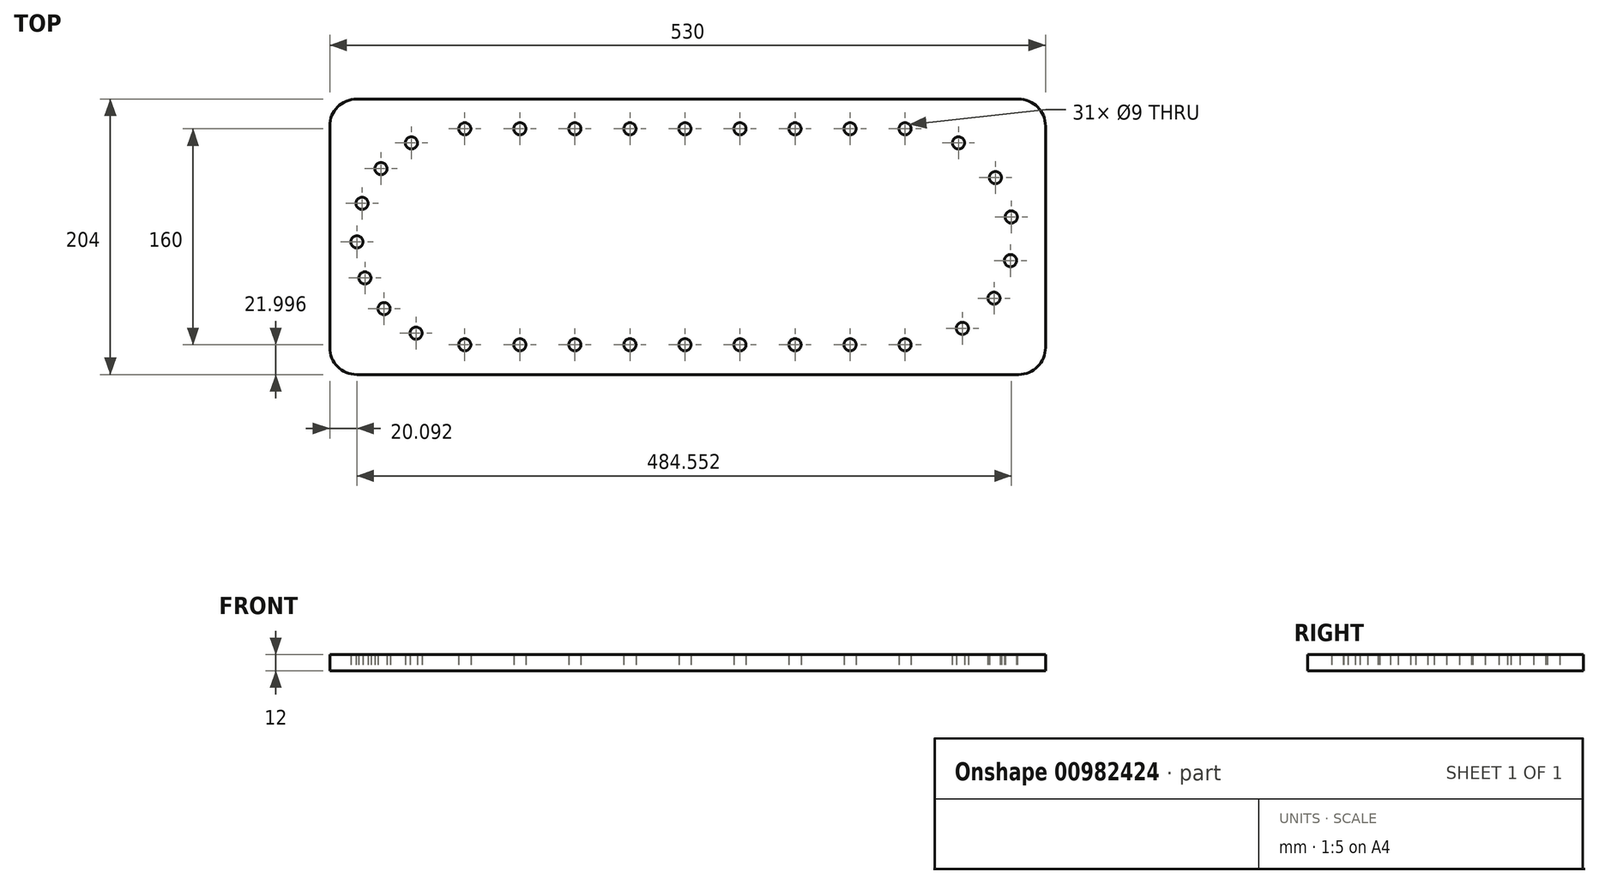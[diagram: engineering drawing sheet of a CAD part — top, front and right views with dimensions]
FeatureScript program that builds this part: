
annotation { "Feature Type Name" : "Feature", "Feature Type Description" : "" }
export const myFeature = defineFeature(function(context is Context, id is Id, definition is map)
    precondition{}
    {
        {
            var Q0;
            Q0=qCreatedBy(makeId("Top.planeOp"),FACE);
            var sketch = newSketch(context, id + "F0", { "sketchPlane" : qUnion([Q0])});
            skLineSegment(sketch, "E0.bottom", {"start": v(249.71, 104.58) * mm, "end": v(-240.29, 104.58) * mm});
            skLineSegment(sketch, "E0.top", {"start": v(249.71, -99.42) * mm, "end": v(-240.29, -99.42) * mm});
            skLineSegment(sketch, "E0.left", {"start": v(269.71, 84.58) * mm, "end": v(269.71, -79.42) * mm});
            skLineSegment(sketch, "E0.right", {"start": v(-260.29, 84.58) * mm, "end": v(-260.29, -79.42) * mm});
            skPoint(sketch, "E1", {"position": v(-160.29, 2.58) * mm});
            skPoint(sketch, "E2", {"position": v(165.71, 2.58) * mm});
            skArc(sketch, "E3", {"start": v(165.71, -77.42) * mm, "mid": v(245.71, 2.58) * mm, "end": v(165.71, 82.58) * mm});
            skArc(sketch, "E4", {"start": v(-160.29, 82.58) * mm, "mid": v(-240.29, 2.58) * mm, "end": v(-160.29, -77.42) * mm});
            skPoint(sketch, "E5.visualSharp", {"position": v(-260.29, -99.42) * mm});
            skArc(sketch, "E5.filletArc", {"start": v(-260.29, -79.42) * mm, "mid": v(-254.43, -93.57) * mm, "end": v(-240.29, -99.42) * mm});
            skPoint(sketch, "E6.visualSharp", {"position": v(269.71, -99.42) * mm});
            skArc(sketch, "E6.filletArc", {"start": v(249.71, -99.42) * mm, "mid": v(263.85, -93.57) * mm, "end": v(269.71, -79.42) * mm});
            skPoint(sketch, "E7.visualSharp", {"position": v(269.71, 104.58) * mm});
            skArc(sketch, "E7.filletArc", {"start": v(269.71, 84.58) * mm, "mid": v(263.85, 98.72) * mm, "end": v(249.71, 104.58) * mm});
            skPoint(sketch, "E8.visualSharp", {"position": v(-260.29, 104.58) * mm});
            skArc(sketch, "E8.filletArc", {"start": v(-240.29, 104.58) * mm, "mid": v(-254.43, 98.72) * mm, "end": v(-260.29, 84.58) * mm});
            skLineSegment(sketch, "E9", {"start": v(165.71, -77.42) * mm, "end": v(-160.29, -77.42) * mm});
            skLineSegment(sketch, "E10", {"start": v(-160.29, 82.58) * mm, "end": v(165.71, 82.58) * mm});
            skCircle(sketch, "E11", {"center": v(-160.29, 82.58) * mm, "radius": 4.5 * mm});
            skCircle(sketch, "E12", {"center": v(-160.29, -77.42) * mm, "radius": 4.5 * mm});
            skCircle(sketch, "E13", {"center": v(165.71, -77.42) * mm, "radius": 4.5 * mm});
            skCircle(sketch, "E14", {"center": v(-119.54, 82.58) * mm, "radius": 4.5 * mm});
            skCircle(sketch, "E15", {"center": v(-78.79, 82.58) * mm, "radius": 4.5 * mm});
            skCircle(sketch, "E16", {"center": v(-38.04, 82.58) * mm, "radius": 4.5 * mm});
            skCircle(sketch, "E17", {"center": v(2.71, 82.58) * mm, "radius": 4.5 * mm});
            skCircle(sketch, "E18", {"center": v(43.46, 82.58) * mm, "radius": 4.5 * mm});
            skCircle(sketch, "E19", {"center": v(84.21, 82.58) * mm, "radius": 4.5 * mm});
            skCircle(sketch, "E20", {"center": v(165.71, 82.58) * mm, "radius": 4.5 * mm});
            skCircle(sketch, "E21", {"center": v(124.96, 82.58) * mm, "radius": 4.5 * mm});
            skCircle(sketch, "E22", {"center": v(-119.54, -77.42) * mm, "radius": 4.5 * mm});
            skCircle(sketch, "E23", {"center": v(-78.79, -77.42) * mm, "radius": 4.5 * mm});
            skCircle(sketch, "E24", {"center": v(-38.04, -77.42) * mm, "radius": 4.5 * mm});
            skCircle(sketch, "E25", {"center": v(2.71, -77.42) * mm, "radius": 4.5 * mm});
            skCircle(sketch, "E26", {"center": v(43.46, -77.42) * mm, "radius": 4.5 * mm});
            skCircle(sketch, "E27", {"center": v(84.21, -77.42) * mm, "radius": 4.5 * mm});
            skCircle(sketch, "E28", {"center": v(124.96, -77.42) * mm, "radius": 4.5 * mm});
            skCircle(sketch, "E29", {"center": v(208.14, -65.25) * mm, "radius": 4.5 * mm});
            skCircle(sketch, "E30", {"center": v(231.52, -42.91) * mm, "radius": 4.5 * mm});
            skCircle(sketch, "E31", {"center": v(243.74, -15.05) * mm, "radius": 4.5 * mm});
            skCircle(sketch, "E32", {"center": v(244.35, 17.25) * mm, "radius": 4.5 * mm});
            skCircle(sketch, "E33", {"center": v(232.62, 46.43) * mm, "radius": 4.5 * mm});
            skCircle(sketch, "E34", {"center": v(205.21, 72.14) * mm, "radius": 4.5 * mm});
            skCircle(sketch, "E35", {"center": v(-199.8, 72.14) * mm, "radius": 4.5 * mm});
            skCircle(sketch, "E36", {"center": v(-222.35, 53.06) * mm, "radius": 4.5 * mm});
            skCircle(sketch, "E37", {"center": v(-236.37, 27.31) * mm, "radius": 4.5 * mm});
            skCircle(sketch, "E38", {"center": v(-240.2, -1.24) * mm, "radius": 4.5 * mm});
            skCircle(sketch, "E39", {"center": v(-234.24, -27.94) * mm, "radius": 4.5 * mm});
            skCircle(sketch, "E40", {"center": v(-196.41, -68.8) * mm, "radius": 4.5 * mm});
            skCircle(sketch, "E41", {"center": v(-220.01, -50.65) * mm, "radius": 4.5 * mm});
            skSolve(sketch);
        }
        {
            var Q0;
            Q0=makeQuery(id+"F0.imprint","IMPRINT",FACE,{"disambiguationData":[TD([[makeQuery(id+"F0.imprint","IMPRINT",EDGE,{"derivedFrom":sQuery(id+"F0.wireOp",EDGE,"E0.bottom")}),1.0]])]});
            var Q1;
            {var subQ19=sQuery(id+"F0.wireOp",EDGE,"E13");var subQ20=sQuery(id+"F0.wireOp",EDGE,"E3");var subQ21=makeQuery(id+"F0.imprint","INTERSECT",VERTEX,{"derivedFrom":[subQ20,subQ19]});Q1=makeQuery(id+"F0.imprint","IMPRINT",FACE,{"disambiguationData":[TD([[makeQuery(id+"F0.imprint","IMPRINT",EDGE,{"disambiguationData":[TD([[subQ21,-1.0]])],"derivedFrom":subQ20}),1.0]])]});}
            extrude(context, id + "F1", {"entities" : qUnion([Q0, Q1]), "depth" : 12 * mm, "offsetDistance" : 25 * mm});
        }
    });
